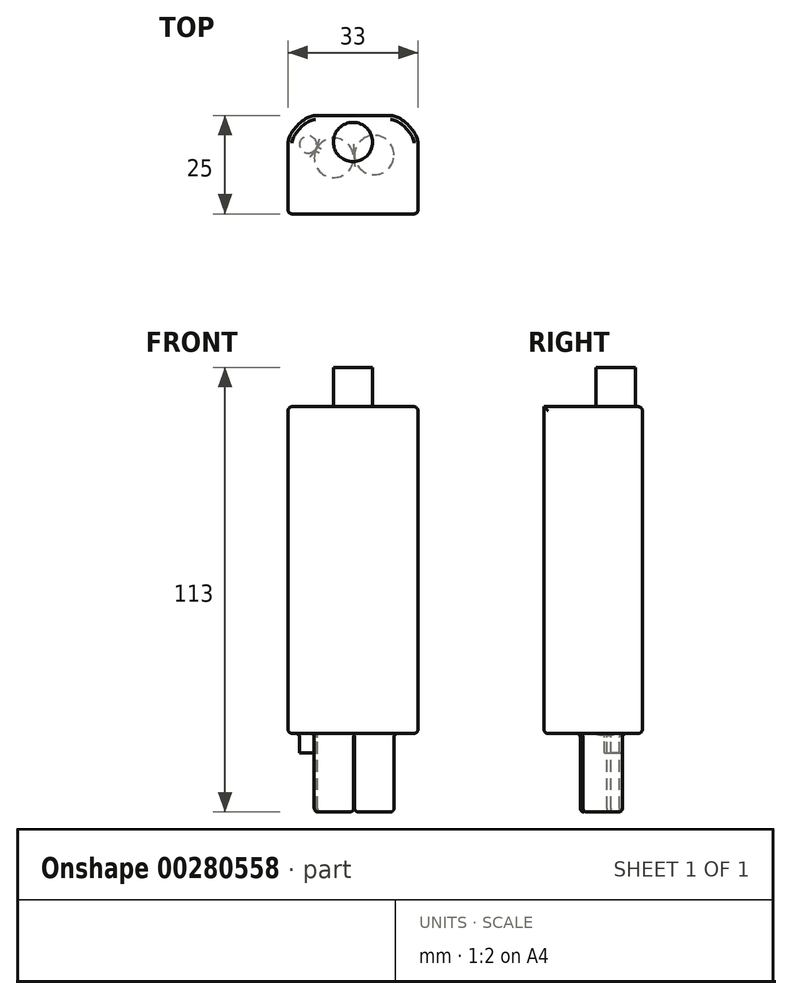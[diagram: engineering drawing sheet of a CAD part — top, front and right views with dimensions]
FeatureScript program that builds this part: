
annotation { "Feature Type Name" : "Feature", "Feature Type Description" : "" }
export const myFeature = defineFeature(function(context is Context, id is Id, definition is map)
    precondition{}
    {
        {
            var Q0;
            Q0=qCreatedBy(makeId("Front.planeOp"),FACE);
            var sketch = newSketch(context, id + "F0", { "sketchPlane" : qUnion([Q0])});
            skLineSegment(sketch, "E0.bottom", {"start": v(16.5, 41.5) * mm, "end": v(-16.5, 41.5) * mm});
            skLineSegment(sketch, "E0.top", {"start": v(16.5, -41.5) * mm, "end": v(-16.5, -41.5) * mm});
            skLineSegment(sketch, "E0.left", {"start": v(16.5, 41.5) * mm, "end": v(16.5, -41.5) * mm});
            skLineSegment(sketch, "E0.right", {"start": v(-16.5, 41.5) * mm, "end": v(-16.5, -41.5) * mm});
            skPoint(sketch, "E0.middle", {"position": v(0, 0) * mm});
            skSolve(sketch);
        }
        {
            var Q0;
            Q0 = qSketchRegion(id + "F0", true);
            extrude(context, id + "F1", {"entities" : qUnion([Q0]), "depth" : 25 * mm});
        }
        {
            var Q0;
            Q0=makeQuery(id+"F1.opExtrude","SWEPT_FACE",FACE,{"disambiguationData":[OSD([sQuery(id+"F0.wireOp",EDGE,"E0.top")])]});
            var sketch = newSketch(context, id + "F2", { "sketchPlane" : qUnion([Q0])});
            skCircle(sketch, "E1", {"center": v(-4.85, 10.76) * mm, "radius": 5 * mm});
            skCircle(sketch, "E2", {"center": v(5.41, 10.06) * mm, "radius": 5 * mm});
            skCircle(sketch, "E3", {"center": v(-11.4, 7.39) * mm, "radius": 2.45 * mm});
            skCircle(sketch, "E4", {"center": v(11.6, 6.6) * mm, "radius": 2.09 * mm});
            skSolve(sketch);
        }
        {
            var Q0;
            Q0=makeQuery(id+"F2.imprint","IMPRINT",FACE,{"disambiguationData":[TD([[makeQuery(id+"F2.imprint","IMPRINT",EDGE,{"derivedFrom":sQuery(id+"F2.wireOp",EDGE,"E2")}),1.0]])]});
            var Q1;
            {var subQ0=sQuery(id+"F2.wireOp",EDGE,"E3");var subQ1=sQuery(id+"F2.wireOp",EDGE,"E1");var subQ2=makeQuery(id+"F2.imprint","INTERSECT",VERTEX,{"disambiguationData":[OD(0.0)],"derivedFrom":[subQ1,subQ0]});Q1=makeQuery(id+"F2.imprint","IMPRINT",FACE,{"disambiguationData":[TD([[makeQuery(id+"F2.imprint","IMPRINT",EDGE,{"disambiguationData":[TD([[subQ2,1.0]])],"derivedFrom":subQ1}),1.0]])]});}
            extrude(context, id + "F3", {"entities" : qUnion([Q0, Q1]), "operationType" : NewBodyOperationType.ADD, "depth" : 20 * mm});
        }
        {
            var Q0;
            Q0=makeQuery(id+"F1.opExtrude","CAP_EDGE",EDGE,{"disambiguationData":[OSD([sQuery(id+"F0.wireOp",EDGE,"E0.right")])],"isStart":true});
            var Q1;
            Q1=makeQuery(id+"F1.opExtrude","CAP_EDGE",EDGE,{"disambiguationData":[OSD([sQuery(id+"F0.wireOp",EDGE,"E0.left")])],"isStart":true});
            fillet(context, id + "F4", {"entities" : qUnion([Q0, Q1]), "radius" : 7 * mm, "rho" : 0.3, "crossSection" : FilletCrossSection.CONIC, "allowEdgeOverflow" : false});
        }
        {
            var Q0;
            Q0=makeQuery(id+"F1.opExtrude","SWEPT_FACE",FACE,{"disambiguationData":[OSD([sQuery(id+"F0.wireOp",EDGE,"E0.bottom")])]});
            var sketch = newSketch(context, id + "F5", { "sketchPlane" : qUnion([Q0])});
            skCircle(sketch, "E5", {"center": v(0, -6.76) * mm, "radius": 4.99 * mm});
            skSolve(sketch);
        }
        {
            var Q0;
            Q0 = qSketchRegion(id + "F5", true);
            extrude(context, id + "F6", {"entities" : qUnion([Q0]), "operationType" : NewBodyOperationType.ADD, "depth" : 10 * mm});
        }
        {
            var Q0;
            Q0=makeQuery(id+"F1.opExtrude","SWEPT_FACE",FACE,{"disambiguationData":[OSD([sQuery(id+"F0.wireOp",EDGE,"E0.top")])]});
            var sketch = newSketch(context, id + "F7", { "sketchPlane" : qUnion([Q0])});
            skCircle(sketch, "E6", {"center": v(-11.4, 7.39) * mm, "radius": 2.18 * mm});
            skCircle(sketch, "E7.MirrorC", {"center": v(11.4, 7.39) * mm, "radius": 2.18 * mm});
            skSolve(sketch);
        }
        {
            var Q0;
            Q0=makeQuery(id+"F7.imprint","IMPRINT",FACE,{"disambiguationData":[TD([[makeQuery(id+"F7.imprint","IMPRINT",EDGE,{"derivedFrom":sQuery(id+"F7.wireOp",EDGE,"E6")}),1.0]])]});
            var Q1;
            {var subQ0=sQuery(id+"F7.wireOp",EDGE,"E7.MirrorC");var subQ1=makeQuery(id+"F3.opExtrude","CAP_EDGE",EDGE,{"disambiguationData":[OSD([sQuery(id+"F2.wireOp",EDGE,"E2")])],"isStart":true});var subQ2=makeQuery(id+"F7.imprint","INTERSECT",VERTEX,{"disambiguationData":[OD(0.0)],"derivedFrom":[subQ1,subQ0]});Q1=makeQuery(id+"F7.imprint","IMPRINT",FACE,{"disambiguationData":[TD([[makeQuery(id+"F7.imprint","IMPRINT",EDGE,{"disambiguationData":[TD([[subQ2,-1.0]])],"derivedFrom":subQ0}),-1.0]])]});}
            extrude(context, id + "F8", {"entities" : qUnion([Q0, Q1]), "operationType" : NewBodyOperationType.ADD, "depth" : 5 * mm});
        }
        {
            var Q0;
            Q0=makeQuery(id+"F1.opExtrude","CAP_EDGE",EDGE,{"disambiguationData":[OSD([sQuery(id+"F0.wireOp",EDGE,"E0.left")])],"isStart":false});
            var Q1;
            Q1=makeQuery(id+"F1.opExtrude","CAP_EDGE",EDGE,{"disambiguationData":[OSD([sQuery(id+"F0.wireOp",EDGE,"E0.right")])],"isStart":false});
            var Q2;
            Q2=makeQuery(id+"F1.opExtrude","SWEPT_FACE",FACE,{"disambiguationData":[OSD([sQuery(id+"F0.wireOp",EDGE,"E0.top")])]});
            var Q3;
            Q3=makeQuery(id+"F3.opExtrude","CAP_FACE",FACE,{"disambiguationData":[OSD([sQuery(id+"F2.wireOp",EDGE,"E1"),sQuery(id+"F2.wireOp",EDGE,"E3")])],"isStart":false});
            var Q4;
            Q4=makeQuery(id+"F3.opExtrude","CAP_FACE",FACE,{"disambiguationData":[OSD([sQuery(id+"F2.wireOp",EDGE,"E2")])],"isStart":false});
            var Q5;
            Q5=makeQuery(id+"F4.opFillet","BLEND_EDGE",EDGE,{"blendedFrom":[makeQuery(id+"F1.opExtrude","CAP_EDGE",EDGE,{"disambiguationData":[OSD([sQuery(id+"F0.wireOp",EDGE,"E0.left")])],"isStart":true}),makeQuery(id+"F1.opExtrude","SWEPT_FACE",FACE,{"disambiguationData":[OSD([sQuery(id+"F0.wireOp",EDGE,"E0.bottom")])]})],"blendedInto":[makeQuery(id+"F1.opExtrude","SWEPT_FACE",FACE,{"disambiguationData":[OSD([sQuery(id+"F0.wireOp",EDGE,"E0.bottom")])]})]});
            var Q6;
            Q6=makeQuery(id+"F1.opExtrude","CAP_EDGE",EDGE,{"disambiguationData":[OSD([sQuery(id+"F0.wireOp",EDGE,"E0.bottom")])],"isStart":true});
            fillet(context, id + "F9", {"entities" : qUnion([Q0, Q1, Q2, Q3, Q4, Q5, Q6]), "radius" : 1 * mm, "tangentPropagation" : true, "allowEdgeOverflow" : false});
        }
    });
